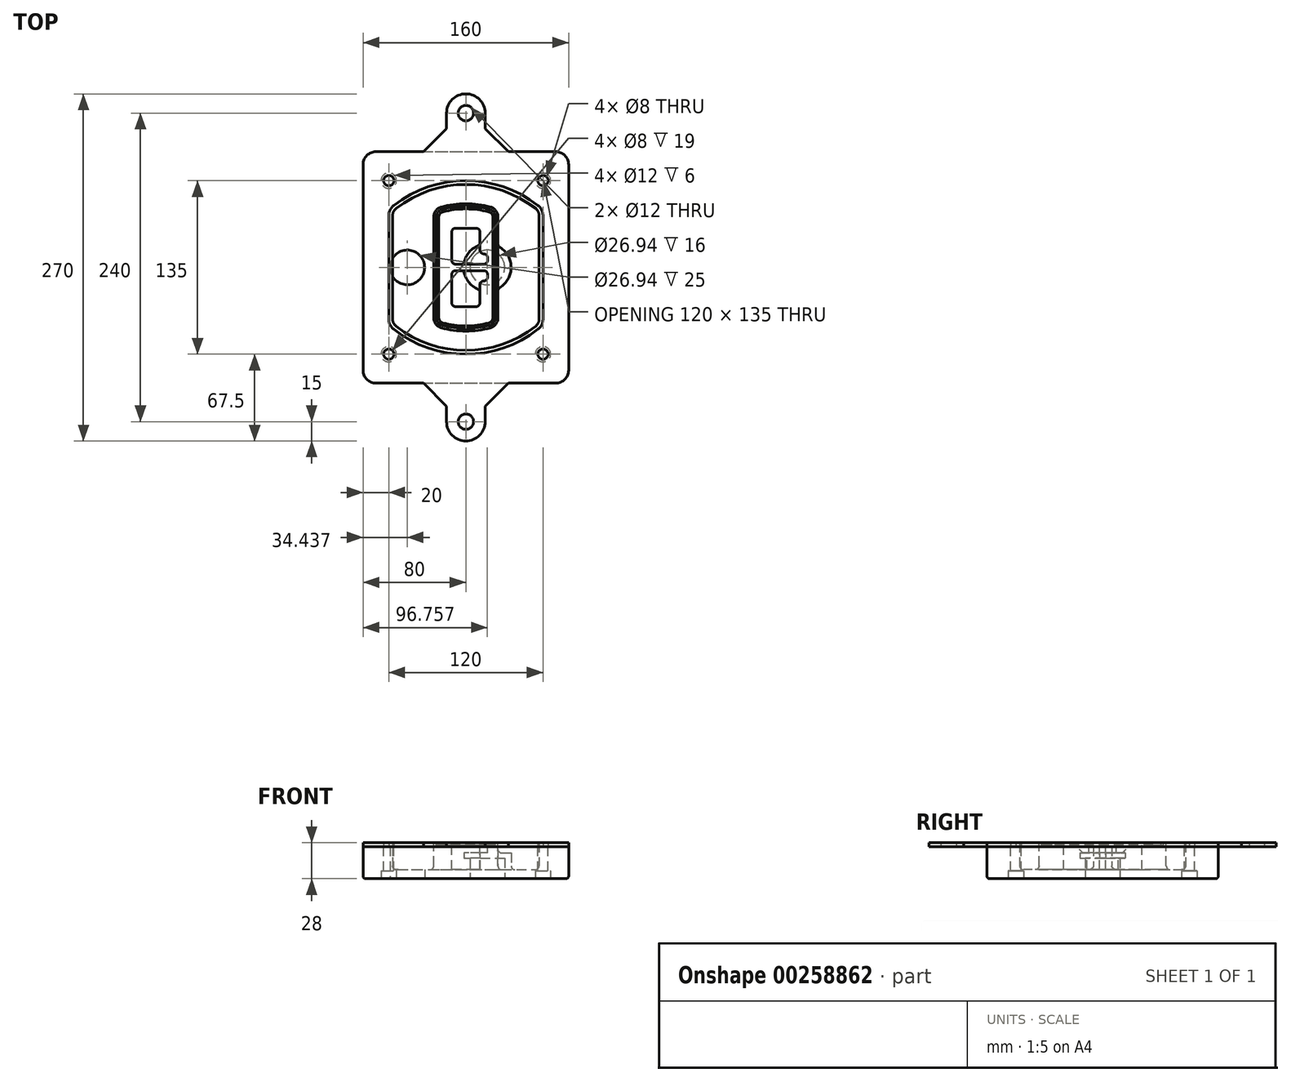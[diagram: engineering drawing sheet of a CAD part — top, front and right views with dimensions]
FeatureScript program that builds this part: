
annotation { "Feature Type Name" : "Feature", "Feature Type Description" : "" }
export const myFeature = defineFeature(function(context is Context, id is Id, definition is map)
    precondition{}
    {
        {
            var Q0;
            Q0=qCreatedBy(makeId("Top.planeOp"),FACE);
            var sketch = newSketch(context, id + "F0", { "sketchPlane" : qUnion([Q0])});
            skPoint(sketch, "E0.rect.middle", {"position": v(0, 0) * mm});
            skLineSegment(sketch, "E1.bottom", {"start": v(-70, -90) * mm, "end": v(70, -90) * mm});
            skLineSegment(sketch, "E1.top", {"start": v(-70, 90) * mm, "end": v(70, 90) * mm});
            skLineSegment(sketch, "E1.left", {"start": v(-80, -80) * mm, "end": v(-80, 80) * mm});
            skLineSegment(sketch, "E1.right", {"start": v(80, -80) * mm, "end": v(80, 80) * mm});
            skLineSegment(sketch, "E2", {"start": v(-80, 90) * mm, "end": v(80, -90) * mm, "construction": true});
            skLineSegment(sketch, "E3", {"start": v(80, 90) * mm, "end": v(-80, -90) * mm, "construction": true});
            skCircle(sketch, "E4", {"center": v(-60, 67.5) * mm, "radius": 4 * mm});
            skCircle(sketch, "E5", {"center": v(60, 67.5) * mm, "radius": 4 * mm});
            skCircle(sketch, "E6", {"center": v(60, -67.5) * mm, "radius": 4 * mm});
            skCircle(sketch, "E7", {"center": v(-60, -67.5) * mm, "radius": 4 * mm});
            skLineSegment(sketch, "E8", {"start": v(-60, 67.5) * mm, "end": v(60, 67.5) * mm, "construction": true});
            skLineSegment(sketch, "E9", {"start": v(60, 67.5) * mm, "end": v(60, -67.5) * mm, "construction": true});
            skLineSegment(sketch, "E10", {"start": v(60, -67.5) * mm, "end": v(-60, -67.5) * mm, "construction": true});
            skLineSegment(sketch, "E11", {"start": v(-60, -67.5) * mm, "end": v(-60, 67.5) * mm, "construction": true});
            skLineSegment(sketch, "E12", {"start": v(-60, 40.3) * mm, "end": v(-60, -40.3) * mm});
            skLineSegment(sketch, "E13", {"start": v(60, 40.3) * mm, "end": v(60, -40.3) * mm});
            skArc(sketch, "E14", {"start": v(56.15, 48.18) * mm, "mid": v(0, 67.5) * mm, "end": v(-56.15, 48.18) * mm});
            skArc(sketch, "E15", {"start": v(-56.15, -48.18) * mm, "mid": v(0, -67.5) * mm, "end": v(56.15, -48.18) * mm});
            skLineSegment(sketch, "E16", {"start": v(-60, 0) * mm, "end": v(60, 0) * mm, "construction": true});
            skPoint(sketch, "E17.visualSharp", {"position": v(-60, -45) * mm});
            skArc(sketch, "E17.filletArc", {"start": v(-60, -40.3) * mm, "mid": v(-58.99, -44.68) * mm, "end": v(-56.15, -48.18) * mm});
            skPoint(sketch, "E18.visualSharp", {"position": v(-60, 45) * mm});
            skArc(sketch, "E18.filletArc", {"start": v(-56.15, 48.18) * mm, "mid": v(-58.99, 44.68) * mm, "end": v(-60, 40.3) * mm});
            skPoint(sketch, "E19.visualSharp", {"position": v(60, 45) * mm});
            skArc(sketch, "E19.filletArc", {"start": v(60, 40.3) * mm, "mid": v(58.99, 44.68) * mm, "end": v(56.15, 48.18) * mm});
            skPoint(sketch, "E20.visualSharp", {"position": v(60, -45) * mm});
            skArc(sketch, "E20.filletArc", {"start": v(56.15, -48.18) * mm, "mid": v(58.99, -44.68) * mm, "end": v(60, -40.3) * mm});
            skPoint(sketch, "E21.visualSharp", {"position": v(-80, 90) * mm});
            skArc(sketch, "E21.filletArc", {"start": v(-70, 90) * mm, "mid": v(-77.07, 87.07) * mm, "end": v(-80, 80) * mm});
            skPoint(sketch, "E22.visualSharp", {"position": v(80, 90) * mm});
            skArc(sketch, "E22.filletArc", {"start": v(80, 80) * mm, "mid": v(77.07, 87.07) * mm, "end": v(70, 90) * mm});
            skPoint(sketch, "E23.visualSharp", {"position": v(80, -90) * mm});
            skArc(sketch, "E23.filletArc", {"start": v(70, -90) * mm, "mid": v(77.07, -87.07) * mm, "end": v(80, -80) * mm});
            skPoint(sketch, "E24.visualSharp", {"position": v(-80, -90) * mm});
            skArc(sketch, "E24.filletArc", {"start": v(-80, -80) * mm, "mid": v(-77.07, -87.07) * mm, "end": v(-70, -90) * mm});
            skArc(sketch, "E25.0", {"start": v(57, 40.3) * mm, "mid": v(56.3, 43.36) * mm, "end": v(54.3, 45.81) * mm});
            skLineSegment(sketch, "E25.1", {"start": v(57, 40.3) * mm, "end": v(57, -40.3) * mm});
            skArc(sketch, "E25.2", {"start": v(54.3, -45.81) * mm, "mid": v(56.3, -43.36) * mm, "end": v(57, -40.3) * mm});
            skArc(sketch, "E25.3", {"start": v(-54.3, -45.81) * mm, "mid": v(0, -64.5) * mm, "end": v(54.3, -45.81) * mm});
            skArc(sketch, "E25.4", {"start": v(-57, -40.3) * mm, "mid": v(-56.3, -43.36) * mm, "end": v(-54.3, -45.81) * mm});
            skArc(sketch, "E25.5", {"start": v(54.3, 45.81) * mm, "mid": v(0, 64.5) * mm, "end": v(-54.3, 45.81) * mm});
            skLineSegment(sketch, "E25.6", {"start": v(-57, 40.3) * mm, "end": v(-57, -40.3) * mm});
            skArc(sketch, "E25.7", {"start": v(-54.3, 45.81) * mm, "mid": v(-56.3, 43.36) * mm, "end": v(-57, 40.3) * mm});
            skArc(sketch, "E26.0", {"start": v(-58.62, 51.33) * mm, "mid": v(-62.58, 46.43) * mm, "end": v(-64, 40.3) * mm});
            skArc(sketch, "E26.1", {"start": v(58.62, 51.33) * mm, "mid": v(0, 71.5) * mm, "end": v(-58.62, 51.33) * mm});
            skArc(sketch, "E26.2", {"start": v(64, 40.3) * mm, "mid": v(62.58, 46.43) * mm, "end": v(58.62, 51.33) * mm});
            skLineSegment(sketch, "E26.3", {"start": v(64, 40.3) * mm, "end": v(64, -40.3) * mm});
            skArc(sketch, "E26.4", {"start": v(58.62, -51.33) * mm, "mid": v(62.58, -46.43) * mm, "end": v(64, -40.3) * mm});
            skLineSegment(sketch, "E26.5", {"start": v(-64, 40.3) * mm, "end": v(-64, -40.3) * mm});
            skArc(sketch, "E26.6", {"start": v(-58.62, -51.33) * mm, "mid": v(0, -71.5) * mm, "end": v(58.62, -51.33) * mm});
            skArc(sketch, "E26.7", {"start": v(-64, -40.3) * mm, "mid": v(-62.58, -46.43) * mm, "end": v(-58.62, -51.33) * mm});
            skSolve(sketch);
        }
        {
            var Q0;
            Q0=makeQuery(id+"F0.imprint","IMPRINT",FACE,{"disambiguationData":[TD([[makeQuery(id+"F0.imprint","IMPRINT",EDGE,{"derivedFrom":sQuery(id+"F0.wireOp",EDGE,"E1.bottom")}),1.0]])]});
            var Q1;
            Q1=makeQuery(id+"F0.imprint","IMPRINT",FACE,{"disambiguationData":[TD([[makeQuery(id+"F0.imprint","IMPRINT",EDGE,{"derivedFrom":sQuery(id+"F0.wireOp",EDGE,"E12")}),1.0]])]});
            var Q2;
            Q2=makeQuery(id+"F0.imprint","IMPRINT",FACE,{"disambiguationData":[TD([[makeQuery(id+"F0.imprint","IMPRINT",EDGE,{"derivedFrom":sQuery(id+"F0.wireOp",EDGE,"E25.0")}),1.0]])]});
            var Q3;
            Q3=makeQuery(id+"F0.imprint","IMPRINT",FACE,{"disambiguationData":[TD([[makeQuery(id+"F0.imprint","IMPRINT",EDGE,{"derivedFrom":sQuery(id+"F0.wireOp",EDGE,"E12")}),-1.0]])]});
            extrude(context, id + "F1", {"entities" : qUnion([Q0, Q1, Q2, Q3]), "oppositeDirection" : true, "depth" : 25 * mm});
        }
        {
            var Q0;
            Q0=makeQuery(id+"F0.imprint","IMPRINT",FACE,{"disambiguationData":[TD([[makeQuery(id+"F0.imprint","IMPRINT",EDGE,{"derivedFrom":sQuery(id+"F0.wireOp",EDGE,"E12")}),1.0]])]});
            extrude(context, id + "F2", {"entities" : qUnion([Q0]), "operationType" : NewBodyOperationType.ADD, "depth" : 3 * mm});
        }
        {
            var Q0;
            Q0=makeQuery(id+"F0.imprint","IMPRINT",FACE,{"disambiguationData":[TD([[makeQuery(id+"F0.imprint","IMPRINT",EDGE,{"derivedFrom":sQuery(id+"F0.wireOp",EDGE,"E25.0")}),1.0]])]});
            extrude(context, id + "F3", {"entities" : qUnion([Q0]), "operationType" : NewBodyOperationType.REMOVE, "oppositeDirection" : true, "depth" : 18 * mm});
        }
        {
            var Q0;
            Q0=makeQuery(id+"F2.opExtrude","CAP_FACE",FACE,{"disambiguationData":[OSD([sQuery(id+"F0.wireOp",EDGE,"E12"),sQuery(id+"F0.wireOp",EDGE,"E13"),sQuery(id+"F0.wireOp",EDGE,"E14"),sQuery(id+"F0.wireOp",EDGE,"E15"),sQuery(id+"F0.wireOp",EDGE,"E17.filletArc"),sQuery(id+"F0.wireOp",EDGE,"E18.filletArc"),sQuery(id+"F0.wireOp",EDGE,"E19.filletArc"),sQuery(id+"F0.wireOp",EDGE,"E20.filletArc"),sQuery(id+"F0.wireOp",EDGE,"E25.0"),sQuery(id+"F0.wireOp",EDGE,"E25.1"),sQuery(id+"F0.wireOp",EDGE,"E25.2"),sQuery(id+"F0.wireOp",EDGE,"E25.3"),sQuery(id+"F0.wireOp",EDGE,"E25.4"),sQuery(id+"F0.wireOp",EDGE,"E25.5"),sQuery(id+"F0.wireOp",EDGE,"E25.6"),sQuery(id+"F0.wireOp",EDGE,"E25.7")])],"isStart":false});
            var sketch = newSketch(context, id + "F4", { "sketchPlane" : qUnion([Q0])});
            skArc(sketch, "E27.0", {"start": v(-19.08, -46.97) * mm, "mid": v(0, -49.5) * mm, "end": v(19.08, -46.97) * mm});
            skArc(sketch, "E28.0", {"start": v(19.08, 46.97) * mm, "mid": v(0, 49.5) * mm, "end": v(-19.08, 46.97) * mm});
            skLineSegment(sketch, "E29", {"start": v(-25, 39.25) * mm, "end": v(-25, -39.25) * mm});
            skLineSegment(sketch, "E30", {"start": v(25, 39.25) * mm, "end": v(25, -39.25) * mm});
            skLineSegment(sketch, "E31", {"start": v(-25, 45.1) * mm, "end": v(25, 45.1) * mm, "construction": true});
            skLineSegment(sketch, "E32", {"start": v(-25, -45.1) * mm, "end": v(25, -45.1) * mm, "construction": true});
            skPoint(sketch, "E33.visualSharp", {"position": v(-25, 45.1) * mm});
            skArc(sketch, "E33.filletArc", {"start": v(-19.08, 46.97) * mm, "mid": v(-23.35, 44.11) * mm, "end": v(-25, 39.25) * mm});
            skPoint(sketch, "E34.visualSharp", {"position": v(25, 45.1) * mm});
            skArc(sketch, "E34.filletArc", {"start": v(25, 39.25) * mm, "mid": v(23.35, 44.11) * mm, "end": v(19.08, 46.97) * mm});
            skPoint(sketch, "E35.visualSharp", {"position": v(25, -45.1) * mm});
            skArc(sketch, "E35.filletArc", {"start": v(19.08, -46.97) * mm, "mid": v(23.35, -44.11) * mm, "end": v(25, -39.25) * mm});
            skPoint(sketch, "E36.visualSharp", {"position": v(-25, -45.1) * mm});
            skArc(sketch, "E36.filletArc", {"start": v(-25, -39.25) * mm, "mid": v(-23.35, -44.11) * mm, "end": v(-19.08, -46.97) * mm});
            skArc(sketch, "E37.0", {"start": v(54.3, 45.81) * mm, "mid": v(0, 64.5) * mm, "end": v(-54.3, 45.81) * mm});
            skArc(sketch, "E37.1", {"start": v(-54.3, 45.81) * mm, "mid": v(-56.3, 43.36) * mm, "end": v(-57, 40.3) * mm});
            skLineSegment(sketch, "E37.2", {"start": v(-57, 40.3) * mm, "end": v(-57, -40.3) * mm});
            skArc(sketch, "E37.3", {"start": v(-57, -40.3) * mm, "mid": v(-56.3, -43.36) * mm, "end": v(-54.3, -45.81) * mm});
            skArc(sketch, "E37.4", {"start": v(-54.3, -45.81) * mm, "mid": v(0, -64.5) * mm, "end": v(54.3, -45.81) * mm});
            skArc(sketch, "E37.5", {"start": v(54.3, -45.81) * mm, "mid": v(56.3, -43.36) * mm, "end": v(57, -40.3) * mm});
            skLineSegment(sketch, "E37.6", {"start": v(57, 40.3) * mm, "end": v(57, -40.3) * mm});
            skArc(sketch, "E37.7", {"start": v(57, 40.3) * mm, "mid": v(56.3, 43.36) * mm, "end": v(54.3, 45.81) * mm});
            skLineSegment(sketch, "E38.0", {"start": v(23, 39.25) * mm, "end": v(23, -39.25) * mm});
            skArc(sketch, "E38.1", {"start": v(18.56, -45.04) * mm, "mid": v(21.76, -42.9) * mm, "end": v(23, -39.25) * mm});
            skArc(sketch, "E38.2", {"start": v(-18.56, -45.04) * mm, "mid": v(0, -47.5) * mm, "end": v(18.56, -45.04) * mm});
            skArc(sketch, "E38.3", {"start": v(-23, -39.25) * mm, "mid": v(-21.76, -42.9) * mm, "end": v(-18.56, -45.04) * mm});
            skLineSegment(sketch, "E38.4", {"start": v(-23, 39.25) * mm, "end": v(-23, -39.25) * mm});
            skArc(sketch, "E38.5", {"start": v(23, 39.25) * mm, "mid": v(21.76, 42.9) * mm, "end": v(18.56, 45.04) * mm});
            skArc(sketch, "E38.6", {"start": v(-18.56, 45.04) * mm, "mid": v(-21.76, 42.9) * mm, "end": v(-23, 39.25) * mm});
            skArc(sketch, "E38.7", {"start": v(18.56, 45.04) * mm, "mid": v(0, 47.5) * mm, "end": v(-18.56, 45.04) * mm});
            skArc(sketch, "E39.0", {"start": v(21, 39.25) * mm, "mid": v(20.18, 41.68) * mm, "end": v(18.04, 43.1) * mm});
            skLineSegment(sketch, "E39.1", {"start": v(21, 39.25) * mm, "end": v(21, -39.25) * mm});
            skArc(sketch, "E39.2", {"start": v(18.04, -43.1) * mm, "mid": v(20.18, -41.68) * mm, "end": v(21, -39.25) * mm});
            skArc(sketch, "E39.3", {"start": v(-18.04, -43.1) * mm, "mid": v(0, -45.5) * mm, "end": v(18.04, -43.1) * mm});
            skArc(sketch, "E39.4", {"start": v(-21, -39.25) * mm, "mid": v(-20.18, -41.68) * mm, "end": v(-18.04, -43.1) * mm});
            skArc(sketch, "E39.5", {"start": v(18.04, 43.1) * mm, "mid": v(0, 45.5) * mm, "end": v(-18.04, 43.1) * mm});
            skLineSegment(sketch, "E39.6", {"start": v(-21, 39.25) * mm, "end": v(-21, -39.25) * mm});
            skArc(sketch, "E39.7", {"start": v(-18.04, 43.1) * mm, "mid": v(-20.18, 41.68) * mm, "end": v(-21, 39.25) * mm});
            skLineSegment(sketch, "E40", {"start": v(-25, 0) * mm, "end": v(25, 0) * mm, "construction": true});
            skLineSegment(sketch, "E41", {"start": v(-11, 5.5) * mm, "end": v(-11, 27.5) * mm});
            skLineSegment(sketch, "E42", {"start": v(-8, 30.5) * mm, "end": v(8, 30.5) * mm});
            skLineSegment(sketch, "E43", {"start": v(11, 27.5) * mm, "end": v(11, 13.5) * mm});
            skLineSegment(sketch, "E44", {"start": v(14, 10.5) * mm, "end": v(14, 10.5) * mm});
            skLineSegment(sketch, "E45", {"start": v(17, 7.5) * mm, "end": v(17, 5.5) * mm});
            skLineSegment(sketch, "E46", {"start": v(14, 2.5) * mm, "end": v(-8, 2.5) * mm});
            skPoint(sketch, "E47.visualSharp", {"position": v(-11, 30.5) * mm});
            skArc(sketch, "E47.filletArc", {"start": v(-8, 30.5) * mm, "mid": v(-10.12, 29.62) * mm, "end": v(-11, 27.5) * mm});
            skPoint(sketch, "E48.visualSharp", {"position": v(11, 30.5) * mm});
            skArc(sketch, "E48.filletArc", {"start": v(11, 27.5) * mm, "mid": v(10.12, 29.62) * mm, "end": v(8, 30.5) * mm});
            skPoint(sketch, "E49.visualSharp", {"position": v(11, 10.5) * mm});
            skArc(sketch, "E49.filletArc", {"start": v(11, 13.5) * mm, "mid": v(11.88, 11.38) * mm, "end": v(14, 10.5) * mm});
            skPoint(sketch, "E50.visualSharp", {"position": v(17, 10.5) * mm});
            skArc(sketch, "E50.filletArc", {"start": v(17, 7.5) * mm, "mid": v(16.12, 9.62) * mm, "end": v(14, 10.5) * mm});
            skPoint(sketch, "E51.visualSharp", {"position": v(17, 2.5) * mm});
            skArc(sketch, "E51.filletArc", {"start": v(14, 2.5) * mm, "mid": v(16.12, 3.38) * mm, "end": v(17, 5.5) * mm});
            skPoint(sketch, "E52.visualSharp", {"position": v(-11, 2.5) * mm});
            skArc(sketch, "E52.filletArc", {"start": v(-11, 5.5) * mm, "mid": v(-10.12, 3.38) * mm, "end": v(-8, 2.5) * mm});
            skLineSegment(sketch, "E53.0.MirrorCS", {"start": v(14, -2.5) * mm, "end": v(-8, -2.5) * mm});
            skArc(sketch, "E54.0.MirrorCS", {"start": v(-11, -5.5) * mm, "mid": v(-10.12, -3.38) * mm, "end": v(-8, -2.5) * mm});
            skLineSegment(sketch, "E55.0.MirrorCS", {"start": v(-11, -5.5) * mm, "end": v(-11, -27.5) * mm});
            skArc(sketch, "E56.0.MirrorCS", {"start": v(-8, -30.5) * mm, "mid": v(-10.12, -29.62) * mm, "end": v(-11, -27.5) * mm});
            skLineSegment(sketch, "E57.0.MirrorCS", {"start": v(-8, -30.5) * mm, "end": v(8, -30.5) * mm});
            skArc(sketch, "E58.0.MirrorCS", {"start": v(11, -27.5) * mm, "mid": v(10.12, -29.62) * mm, "end": v(8, -30.5) * mm});
            skLineSegment(sketch, "E59.0.MirrorCS", {"start": v(11, -27.5) * mm, "end": v(11, -13.5) * mm});
            skArc(sketch, "E60.0.MirrorCS", {"start": v(11, -13.5) * mm, "mid": v(11.88, -11.38) * mm, "end": v(14, -10.5) * mm});
            skArc(sketch, "E61.0.MirrorCS", {"start": v(17, -7.5) * mm, "mid": v(16.12, -9.62) * mm, "end": v(14, -10.5) * mm});
            skLineSegment(sketch, "E62.0.MirrorCS", {"start": v(17, -7.5) * mm, "end": v(17, -5.5) * mm});
            skArc(sketch, "E63.0.MirrorCS", {"start": v(14, -2.5) * mm, "mid": v(16.12, -3.38) * mm, "end": v(17, -5.5) * mm});
            skSolve(sketch);
        }
        {
            var Q0;
            Q0=makeQuery(id+"F4.imprint","IMPRINT",FACE,{"disambiguationData":[TD([[makeQuery(id+"F4.imprint","IMPRINT",EDGE,{"derivedFrom":sQuery(id+"F4.wireOp",EDGE,"E27.0")}),1.0]])]});
            var Q1;
            Q1=makeQuery(id+"F4.imprint","IMPRINT",FACE,{"disambiguationData":[TD([[makeQuery(id+"F4.imprint","IMPRINT",EDGE,{"derivedFrom":sQuery(id+"F4.wireOp",EDGE,"E38.0")}),-1.0]])]});
            var Q2;
            Q2=makeQuery(id+"F4.imprint","IMPRINT",FACE,{"disambiguationData":[TD([[makeQuery(id+"F4.imprint","IMPRINT",EDGE,{"derivedFrom":sQuery(id+"F4.wireOp",EDGE,"E39.0")}),1.0]])]});
            extrude(context, id + "F5", {"entities" : qUnion([Q0, Q1, Q2]), "operationType" : NewBodyOperationType.ADD, "endBound" : BoundingType.UP_TO_NEXT, "oppositeDirection" : true, "depth" : 25 * mm});
        }
        {
            var Q0;
            Q0=makeQuery(id+"F4.imprint","IMPRINT",FACE,{"disambiguationData":[TD([[makeQuery(id+"F4.imprint","IMPRINT",EDGE,{"derivedFrom":sQuery(id+"F4.wireOp",EDGE,"E38.0")}),-1.0]])]});
            extrude(context, id + "F6", {"entities" : qUnion([Q0]), "operationType" : NewBodyOperationType.REMOVE, "oppositeDirection" : true, "depth" : 2 * mm});
        }
        {
            var Q0;
            Q0=makeQuery(id+"F1.opExtrude","CAP_FACE",FACE,{"disambiguationData":[OSD([sQuery(id+"F0.wireOp",EDGE,"E1.bottom"),sQuery(id+"F0.wireOp",EDGE,"E1.top"),sQuery(id+"F0.wireOp",EDGE,"E1.left"),sQuery(id+"F0.wireOp",EDGE,"E1.right"),sQuery(id+"F0.wireOp",EDGE,"E4"),sQuery(id+"F0.wireOp",EDGE,"E5"),sQuery(id+"F0.wireOp",EDGE,"E6"),sQuery(id+"F0.wireOp",EDGE,"E7"),sQuery(id+"F0.wireOp",EDGE,"E21.filletArc"),sQuery(id+"F0.wireOp",EDGE,"E22.filletArc"),sQuery(id+"F0.wireOp",EDGE,"E23.filletArc"),sQuery(id+"F0.wireOp",EDGE,"E24.filletArc")])],"isStart":false});
            var sketch = newSketch(context, id + "F7", { "sketchPlane" : qUnion([Q0])});
            skCircle(sketch, "E64", {"center": v(16.76, 0) * mm, "radius": 13.47 * mm});
            skCircle(sketch, "E65", {"center": v(-45.56, 0) * mm, "radius": 13.47 * mm});
            skLineSegment(sketch, "E66", {"start": v(80, 0) * mm, "end": v(-80, 0) * mm});
            skCircle(sketch, "E67", {"center": v(16.76, 0) * mm, "radius": 18.47 * mm});
            skCircle(sketch, "E68", {"center": v(60, -67.5) * mm, "radius": 6 * mm});
            skCircle(sketch, "E69", {"center": v(-60, -67.5) * mm, "radius": 6 * mm});
            skCircle(sketch, "E70", {"center": v(-60, 67.5) * mm, "radius": 6 * mm});
            skCircle(sketch, "E71", {"center": v(60, 67.5) * mm, "radius": 6 * mm});
            skSolve(sketch);
        }
        {
            var Q0;
            {var subQ1=sQuery(id+"F7.wireOp",EDGE,"E66");var subQ4=sQuery(id+"F7.wireOp",EDGE,"E64");var subQ6=makeQuery(id+"F7.imprint","INTERSECT",VERTEX,{"disambiguationData":[OD(0.0)],"derivedFrom":[subQ4,subQ1]});Q0=makeQuery(id+"F7.imprint","IMPRINT",FACE,{"disambiguationData":[TD([[makeQuery(id+"F7.imprint","IMPRINT",EDGE,{"disambiguationData":[TD([[subQ6,-1.0]])],"derivedFrom":subQ4}),-1.0]])]});}
            var Q1;
            {var subQ0=sQuery(id+"F7.wireOp",EDGE,"E66");var subQ1=sQuery(id+"F7.wireOp",EDGE,"E64");var subQ3=makeQuery(id+"F7.imprint","INTERSECT",VERTEX,{"disambiguationData":[OD(0.0)],"derivedFrom":[subQ1,subQ0]});Q1=makeQuery(id+"F7.imprint","IMPRINT",FACE,{"disambiguationData":[TD([[makeQuery(id+"F7.imprint","IMPRINT",EDGE,{"disambiguationData":[TD([[subQ3,-1.0]])],"derivedFrom":subQ1}),1.0]])]});}
            var Q2;
            {var subQ0=sQuery(id+"F7.wireOp",EDGE,"E66");var subQ1=sQuery(id+"F7.wireOp",EDGE,"E64");var subQ3=makeQuery(id+"F7.imprint","INTERSECT",VERTEX,{"disambiguationData":[OD(0.0)],"derivedFrom":[subQ1,subQ0]});Q2=makeQuery(id+"F7.imprint","IMPRINT",FACE,{"disambiguationData":[TD([[makeQuery(id+"F7.imprint","IMPRINT",EDGE,{"disambiguationData":[TD([[subQ3,1.0]])],"derivedFrom":subQ1}),1.0]])]});}
            var Q3;
            {var subQ1=sQuery(id+"F7.wireOp",EDGE,"E66");var subQ4=sQuery(id+"F7.wireOp",EDGE,"E64");var subQ6=makeQuery(id+"F7.imprint","INTERSECT",VERTEX,{"disambiguationData":[OD(0.0)],"derivedFrom":[subQ4,subQ1]});Q3=makeQuery(id+"F7.imprint","IMPRINT",FACE,{"disambiguationData":[TD([[makeQuery(id+"F7.imprint","IMPRINT",EDGE,{"disambiguationData":[TD([[subQ6,1.0]])],"derivedFrom":subQ4}),-1.0]])]});}
            extrude(context, id + "F8", {"entities" : qUnion([Q0, Q1, Q2, Q3]), "operationType" : NewBodyOperationType.ADD, "oppositeDirection" : true, "depth" : 20 * mm});
        }
        {
            var Q0;
            {var subQ0=sQuery(id+"F7.wireOp",EDGE,"E66");var subQ1=sQuery(id+"F7.wireOp",EDGE,"E64");var subQ3=makeQuery(id+"F7.imprint","INTERSECT",VERTEX,{"disambiguationData":[OD(0.0)],"derivedFrom":[subQ1,subQ0]});Q0=makeQuery(id+"F7.imprint","IMPRINT",FACE,{"disambiguationData":[TD([[makeQuery(id+"F7.imprint","IMPRINT",EDGE,{"disambiguationData":[TD([[subQ3,-1.0]])],"derivedFrom":subQ1}),1.0]])]});}
            var Q1;
            {var subQ0=sQuery(id+"F7.wireOp",EDGE,"E66");var subQ1=sQuery(id+"F7.wireOp",EDGE,"E64");var subQ3=makeQuery(id+"F7.imprint","INTERSECT",VERTEX,{"disambiguationData":[OD(0.0)],"derivedFrom":[subQ1,subQ0]});Q1=makeQuery(id+"F7.imprint","IMPRINT",FACE,{"disambiguationData":[TD([[makeQuery(id+"F7.imprint","IMPRINT",EDGE,{"disambiguationData":[TD([[subQ3,1.0]])],"derivedFrom":subQ1}),1.0]])]});}
            extrude(context, id + "F9", {"entities" : qUnion([Q0, Q1]), "operationType" : NewBodyOperationType.REMOVE, "oppositeDirection" : true, "depth" : 16 * mm});
        }
        {
            var Q0;
            {var subQ0=sQuery(id+"F7.wireOp",EDGE,"E66");var subQ1=sQuery(id+"F7.wireOp",EDGE,"E65");var subQ3=makeQuery(id+"F7.imprint","INTERSECT",VERTEX,{"disambiguationData":[OD(0.0)],"derivedFrom":[subQ1,subQ0]});Q0=makeQuery(id+"F7.imprint","IMPRINT",FACE,{"disambiguationData":[TD([[makeQuery(id+"F7.imprint","IMPRINT",EDGE,{"disambiguationData":[TD([[subQ3,-1.0]])],"derivedFrom":subQ1}),1.0]])]});}
            var Q1;
            {var subQ0=sQuery(id+"F7.wireOp",EDGE,"E66");var subQ1=sQuery(id+"F7.wireOp",EDGE,"E65");var subQ3=makeQuery(id+"F7.imprint","INTERSECT",VERTEX,{"disambiguationData":[OD(0.0)],"derivedFrom":[subQ1,subQ0]});Q1=makeQuery(id+"F7.imprint","IMPRINT",FACE,{"disambiguationData":[TD([[makeQuery(id+"F7.imprint","IMPRINT",EDGE,{"disambiguationData":[TD([[subQ3,1.0]])],"derivedFrom":subQ1}),1.0]])]});}
            extrude(context, id + "F10", {"entities" : qUnion([Q0, Q1]), "operationType" : NewBodyOperationType.REMOVE, "oppositeDirection" : true, "depth" : 25 * mm});
        }
        {
            var Q0;
            Q0=makeQuery(id+"F7.imprint","IMPRINT",FACE,{"disambiguationData":[TD([[makeQuery(id+"F7.imprint","IMPRINT",EDGE,{"derivedFrom":sQuery(id+"F7.wireOp",EDGE,"E68")}),1.0]])]});
            var Q1;
            Q1=makeQuery(id+"F7.imprint","IMPRINT",FACE,{"disambiguationData":[TD([[makeQuery(id+"F7.imprint","IMPRINT",EDGE,{"derivedFrom":makeQuery(id+"F1.opExtrude","CAP_EDGE",EDGE,{"disambiguationData":[OSD([sQuery(id+"F0.wireOp",EDGE,"E5")])],"isStart":false})}),-1.0]])]});
            var Q2;
            Q2=makeQuery(id+"F7.imprint","IMPRINT",FACE,{"disambiguationData":[TD([[makeQuery(id+"F7.imprint","IMPRINT",EDGE,{"derivedFrom":sQuery(id+"F7.wireOp",EDGE,"E69")}),1.0]])]});
            var Q3;
            Q3=makeQuery(id+"F7.imprint","IMPRINT",FACE,{"disambiguationData":[TD([[makeQuery(id+"F7.imprint","IMPRINT",EDGE,{"derivedFrom":makeQuery(id+"F1.opExtrude","CAP_EDGE",EDGE,{"disambiguationData":[OSD([sQuery(id+"F0.wireOp",EDGE,"E4")])],"isStart":false})}),-1.0]])]});
            var Q4;
            Q4=makeQuery(id+"F7.imprint","IMPRINT",FACE,{"disambiguationData":[TD([[makeQuery(id+"F7.imprint","IMPRINT",EDGE,{"derivedFrom":sQuery(id+"F7.wireOp",EDGE,"E70")}),1.0]])]});
            var Q5;
            Q5=makeQuery(id+"F7.imprint","IMPRINT",FACE,{"disambiguationData":[TD([[makeQuery(id+"F7.imprint","IMPRINT",EDGE,{"derivedFrom":makeQuery(id+"F1.opExtrude","CAP_EDGE",EDGE,{"disambiguationData":[OSD([sQuery(id+"F0.wireOp",EDGE,"E7")])],"isStart":false})}),-1.0]])]});
            var Q6;
            Q6=makeQuery(id+"F7.imprint","IMPRINT",FACE,{"disambiguationData":[TD([[makeQuery(id+"F7.imprint","IMPRINT",EDGE,{"derivedFrom":sQuery(id+"F7.wireOp",EDGE,"E71")}),1.0]])]});
            var Q7;
            Q7=makeQuery(id+"F7.imprint","IMPRINT",FACE,{"disambiguationData":[TD([[makeQuery(id+"F7.imprint","IMPRINT",EDGE,{"derivedFrom":makeQuery(id+"F1.opExtrude","CAP_EDGE",EDGE,{"disambiguationData":[OSD([sQuery(id+"F0.wireOp",EDGE,"E6")])],"isStart":false})}),-1.0]])]});
            extrude(context, id + "F11", {"entities" : qUnion([Q0, Q1, Q2, Q3, Q4, Q5, Q6, Q7]), "operationType" : NewBodyOperationType.REMOVE, "oppositeDirection" : true, "depth" : 6 * mm});
        }
        {
            var Q0;
            Q0=makeQuery(id+"F9.boolean.opBoolean","COPY",FACE,{"derivedFrom":makeQuery(id+"F9.opExtrude","CAP_FACE",FACE,{"disambiguationData":[OSD([sQuery(id+"F7.wireOp",EDGE,"E64")])],"isStart":false})});
            var sketch = newSketch(context, id + "F12", { "sketchPlane" : qUnion([Q0])});
            skArc(sketch, "E72.0", {"start": v(11, 17.55) * mm, "mid": v(2.57, 11.82) * mm, "end": v(-1.54, 2.5) * mm});
            skArc(sketch, "E72.1", {"start": v(-1.54, -2.5) * mm, "mid": v(2.57, -11.82) * mm, "end": v(11, -17.55) * mm});
            skLineSegment(sketch, "E73", {"start": v(-1.54, -2.5) * mm, "end": v(14, -2.5) * mm});
            skLineSegment(sketch, "E74.0", {"start": v(14, 2.5) * mm, "end": v(-1.54, 2.5) * mm});
            skArc(sketch, "E74.1", {"start": v(14, 2.5) * mm, "mid": v(16.12, 3.38) * mm, "end": v(17, 5.5) * mm});
            skLineSegment(sketch, "E74.2", {"start": v(17, 7.5) * mm, "end": v(17, 5.5) * mm});
            skArc(sketch, "E74.3", {"start": v(17, 7.5) * mm, "mid": v(16.12, 9.62) * mm, "end": v(14, 10.5) * mm});
            skArc(sketch, "E74.4", {"start": v(11, 13.5) * mm, "mid": v(11.88, 11.38) * mm, "end": v(14, 10.5) * mm});
            skLineSegment(sketch, "E74.5", {"start": v(11, 17.55) * mm, "end": v(11, 13.5) * mm});
            skLineSegment(sketch, "E74.7", {"start": v(14, -2.5) * mm, "end": v(-1.54, -2.5) * mm});
            skArc(sketch, "E74.8", {"start": v(14, -2.5) * mm, "mid": v(16.12, -3.38) * mm, "end": v(17, -5.5) * mm});
            skLineSegment(sketch, "E74.9", {"start": v(17, -7.5) * mm, "end": v(17, -5.5) * mm});
            skArc(sketch, "E74.10", {"start": v(17, -7.5) * mm, "mid": v(16.12, -9.62) * mm, "end": v(14, -10.5) * mm});
            skArc(sketch, "E74.11", {"start": v(11, -13.5) * mm, "mid": v(11.88, -11.38) * mm, "end": v(14, -10.5) * mm});
            skLineSegment(sketch, "E74.12", {"start": v(11, -17.55) * mm, "end": v(11, -13.5) * mm});
            skPoint(sketch, "E75.orphan", {"position": v(11, -27.5) * mm});
            skPoint(sketch, "E76.orphan", {"position": v(-8, -2.5) * mm});
            skPoint(sketch, "E77.orphan", {"position": v(-8, 2.5) * mm});
            skPoint(sketch, "E78.orphan", {"position": v(11, 27.5) * mm});
            skSolve(sketch);
        }
        {
            var Q0;
            {var subQ7=sQuery(id+"F12.wireOp",EDGE,"E72.0");var subQ14=sQuery(id+"F12.wireOp",EDGE,"E72.1");var subQ16=sQuery(id+"F12.wireOp",EDGE,"E74.1");var subQ18=sQuery(id+"F12.wireOp",EDGE,"E74.8");Q0=qUnion([makeQuery(id+"F12.imprint","IMPRINT",FACE,{"disambiguationData":[TD([[makeQuery(id+"F12.imprint","IMPRINT",EDGE,{"derivedFrom":subQ7}),1.0]])]}),makeQuery(id+"F12.imprint","IMPRINT",FACE,{"disambiguationData":[TD([[makeQuery(id+"F12.imprint","IMPRINT",EDGE,{"derivedFrom":subQ14}),1.0]])]}),makeQuery(id+"F12.imprint","IMPRINT",FACE,{"disambiguationData":[TD([[makeQuery(id+"F12.imprint","IMPRINT",EDGE,{"derivedFrom":subQ16}),1.0]])]}),makeQuery(id+"F12.imprint","IMPRINT",FACE,{"disambiguationData":[TD([[makeQuery(id+"F12.imprint","IMPRINT",EDGE,{"derivedFrom":subQ18}),-1.0]])]})]);}
            var Q1;
            Q1=makeQuery(id+"F5.boolean.opBoolean","SPLIT",FACE,{"disambiguationData":[TD([makeQuery(id+"F5.opExtrude","SWEPT_FACE",FACE,{"disambiguationData":[OSD([sQuery(id+"F4.wireOp",EDGE,"E41")])]})])],"derivedFrom":makeQuery(id+"F3.boolean.opBoolean","COPY",FACE,{"derivedFrom":makeQuery(id+"F3.opExtrude","CAP_FACE",FACE,{"disambiguationData":[OSD([sQuery(id+"F0.wireOp",EDGE,"E25.0"),sQuery(id+"F0.wireOp",EDGE,"E25.1"),sQuery(id+"F0.wireOp",EDGE,"E25.2"),sQuery(id+"F0.wireOp",EDGE,"E25.3"),sQuery(id+"F0.wireOp",EDGE,"E25.4"),sQuery(id+"F0.wireOp",EDGE,"E25.5"),sQuery(id+"F0.wireOp",EDGE,"E25.6"),sQuery(id+"F0.wireOp",EDGE,"E25.7")])],"isStart":false})})});
            extrude(context, id + "F13", {"entities" : qUnion([Q0]), "operationType" : NewBodyOperationType.REMOVE, "endBound" : BoundingType.UP_TO_SURFACE, "endBoundEntityFace" : qUnion([Q1]), "depth" : 25 * mm});
        }
        {
            var Q0;
            Q0=makeQuery(id+"F3.boolean.opBoolean","COPY",EDGE,{"derivedFrom":makeQuery(id+"F3.opExtrude","CAP_EDGE",EDGE,{"disambiguationData":[OSD([sQuery(id+"F0.wireOp",EDGE,"E25.6")])],"isStart":false})});
            var Q1;
            Q1=makeQuery(id+"F8.boolean.opBoolean","INTERSECT",EDGE,{"derivedFrom":[makeQuery(id+"F5.opExtrude","SWEPT_FACE",FACE,{"disambiguationData":[OSD([sQuery(id+"F4.wireOp",EDGE,"E30")])]}),makeQuery(id+"F8.opExtrude","CAP_FACE",FACE,{"disambiguationData":[OSD([sQuery(id+"F7.wireOp",EDGE,"E67")])],"isStart":false})]});
            var Q2;
            Q2=makeQuery(id+"F8.boolean.opBoolean","INTERSECT",EDGE,{"disambiguationData":[OD(1.0)],"derivedFrom":[makeQuery(id+"F5.opExtrude","SWEPT_FACE",FACE,{"disambiguationData":[OSD([sQuery(id+"F4.wireOp",EDGE,"E30")])]}),makeQuery(id+"F8.opExtrude","SWEPT_FACE",FACE,{"disambiguationData":[OSD([sQuery(id+"F7.wireOp",EDGE,"E67")])]})]});
            var Q3;
            {var subQ0=sQuery(id+"F4.wireOp",EDGE,"E30");Q3=makeQuery(id+"F8.boolean.opBoolean","SPLIT",EDGE,{"disambiguationData":[TD([makeQuery(id+"F5.opExtrude","SWEPT_FACE",FACE,{"disambiguationData":[OSD([sQuery(id+"F4.wireOp",EDGE,"E35.filletArc")])]})])],"derivedFrom":makeQuery(id+"F5.opExtrude","CAP_EDGE",EDGE,{"disambiguationData":[OSD([subQ0])],"isStart":false})});}
            var Q4;
            {var subQ0=sQuery(id+"F0.wireOp",EDGE,"E25.7");var subQ1=sQuery(id+"F0.wireOp",EDGE,"E25.1");var subQ2=sQuery(id+"F0.wireOp",EDGE,"E25.6");var subQ3=sQuery(id+"F0.wireOp",EDGE,"E25.5");var subQ4=sQuery(id+"F0.wireOp",EDGE,"E25.4");var subQ5=sQuery(id+"F0.wireOp",EDGE,"E25.0");var subQ6=sQuery(id+"F0.wireOp",EDGE,"E25.2");var subQ7=sQuery(id+"F0.wireOp",EDGE,"E25.3");Q4=makeQuery(id+"F8.boolean.opBoolean","INTERSECT",EDGE,{"derivedFrom":[makeQuery(id+"F5.boolean.opBoolean","SPLIT",FACE,{"disambiguationData":[TD([makeQuery(id+"F2.opExtrude","SWEPT_FACE",FACE,{"disambiguationData":[OSD([subQ5])]})])],"derivedFrom":makeQuery(id+"F3.boolean.opBoolean","COPY",FACE,{"derivedFrom":makeQuery(id+"F3.opExtrude","CAP_FACE",FACE,{"disambiguationData":[OSD([subQ5,subQ1,subQ6,subQ7,subQ4,subQ3,subQ2,subQ0])],"isStart":false})})}),makeQuery(id+"F8.opExtrude","SWEPT_FACE",FACE,{"disambiguationData":[OSD([sQuery(id+"F7.wireOp",EDGE,"E67")])]})]});}
            var Q5;
            Q5=makeQuery(id+"F8.boolean.opBoolean","INTERSECT",EDGE,{"disambiguationData":[OD(0.0)],"derivedFrom":[makeQuery(id+"F5.opExtrude","SWEPT_FACE",FACE,{"disambiguationData":[OSD([sQuery(id+"F4.wireOp",EDGE,"E30")])]}),makeQuery(id+"F8.opExtrude","SWEPT_FACE",FACE,{"disambiguationData":[OSD([sQuery(id+"F7.wireOp",EDGE,"E67")])]})]});
            fillet(context, id + "F14", {"entities" : qUnion([Q0, Q1, Q2, Q3, Q4, Q5]), "radius" : 3 * mm, "tangentPropagation" : true, "allowEdgeOverflow" : false});
        }
        {
            var Q0;
            Q0=makeQuery(id+"F1.opExtrude","CAP_EDGE",EDGE,{"disambiguationData":[OSD([sQuery(id+"F0.wireOp",EDGE,"E1.bottom")])],"isStart":false});
            fillet(context, id + "F15", {"entities" : qUnion([Q0]), "radius" : 2 * mm, "tangentPropagation" : true, "allowEdgeOverflow" : false});
        }
        {
            var Q0;
            {var subQ0=sQuery(id+"F0.wireOp",EDGE,"E22.filletArc");var subQ1=sQuery(id+"F0.wireOp",EDGE,"E7");var subQ2=sQuery(id+"F0.wireOp",EDGE,"E6");var subQ3=sQuery(id+"F0.wireOp",EDGE,"E5");var subQ4=sQuery(id+"F0.wireOp",EDGE,"E4");var subQ5=sQuery(id+"F0.wireOp",EDGE,"E1.bottom");var subQ6=sQuery(id+"F0.wireOp",EDGE,"E21.filletArc");var subQ7=sQuery(id+"F0.wireOp",EDGE,"E1.top");var subQ8=sQuery(id+"F0.wireOp",EDGE,"E1.left");var subQ9=sQuery(id+"F0.wireOp",EDGE,"E1.right");var subQ10=sQuery(id+"F0.wireOp",EDGE,"E23.filletArc");var subQ11=sQuery(id+"F0.wireOp",EDGE,"E24.filletArc");Q0=makeQuery(id+"F2.boolean.opBoolean","SPLIT",FACE,{"disambiguationData":[TD([makeQuery(id+"F1.opExtrude","SWEPT_FACE",FACE,{"disambiguationData":[OSD([subQ5])]})])],"derivedFrom":makeQuery(id+"F1.opExtrude","CAP_FACE",FACE,{"disambiguationData":[OSD([subQ5,subQ7,subQ8,subQ9,subQ4,subQ3,subQ2,subQ1,subQ6,subQ0,subQ10,subQ11])],"isStart":true})});}
            var sketch = newSketch(context, id + "F16", { "sketchPlane" : qUnion([Q0])});
            skLineSegment(sketch, "E79.0.0", {"start": v(70, 90) * mm, "end": v(-70, 90) * mm});
            skArc(sketch, "E79.0.1", {"start": v(-70, 90) * mm, "mid": v(-77.07, 87.07) * mm, "end": v(-80, 80) * mm});
            skLineSegment(sketch, "E79.0.2", {"start": v(-80, 80) * mm, "end": v(-80, -80) * mm});
            skArc(sketch, "E79.0.3", {"start": v(-80, -80) * mm, "mid": v(-77.07, -87.07) * mm, "end": v(-70, -90) * mm});
            skLineSegment(sketch, "E79.0.4", {"start": v(-70, -90) * mm, "end": v(70, -90) * mm});
            skArc(sketch, "E79.0.5", {"start": v(70, -90) * mm, "mid": v(77.07, -87.07) * mm, "end": v(80, -80) * mm});
            skLineSegment(sketch, "E79.0.6", {"start": v(80, -80) * mm, "end": v(80, 80) * mm});
            skArc(sketch, "E79.0.7", {"start": v(80, 80) * mm, "mid": v(77.07, 87.07) * mm, "end": v(70, 90) * mm});
            skArc(sketch, "E80.0", {"start": v(56.15, 48.18) * mm, "mid": v(0, 67.5) * mm, "end": v(-56.15, 48.18) * mm});
            skArc(sketch, "E81.0", {"start": v(-56.15, 48.18) * mm, "mid": v(-58.99, 44.68) * mm, "end": v(-60, 40.3) * mm});
            skLineSegment(sketch, "E82.0", {"start": v(-60, 40.3) * mm, "end": v(-60, -40.3) * mm});
            skArc(sketch, "E83.0", {"start": v(-60, -40.3) * mm, "mid": v(-58.99, -44.68) * mm, "end": v(-56.15, -48.18) * mm});
            skArc(sketch, "E84.0", {"start": v(-56.15, -48.18) * mm, "mid": v(0, -67.5) * mm, "end": v(56.15, -48.18) * mm});
            skArc(sketch, "E85.0", {"start": v(56.15, -48.18) * mm, "mid": v(58.99, -44.68) * mm, "end": v(60, -40.3) * mm});
            skLineSegment(sketch, "E86.0", {"start": v(60, 40.3) * mm, "end": v(60, -40.3) * mm});
            skLineSegment(sketch, "E87", {"start": v(0, 90) * mm, "end": v(0, 120) * mm, "construction": true});
            skCircle(sketch, "E88", {"center": v(0, 120) * mm, "radius": 6 * mm});
            skLineSegment(sketch, "E89", {"start": v(-33, 90) * mm, "end": v(-15, 108) * mm});
            skLineSegment(sketch, "E90", {"start": v(-15, 108) * mm, "end": v(-15, 120) * mm});
            skArc(sketch, "E91", {"start": v(-15, 120) * mm, "mid": v(0, 135) * mm, "end": v(15, 120) * mm});
            skLineSegment(sketch, "E92", {"start": v(15, 120) * mm, "end": v(15, 108) * mm});
            skLineSegment(sketch, "E93", {"start": v(15, 108) * mm, "end": v(33, 90) * mm});
            skLineSegment(sketch, "E94", {"start": v(-80, 0) * mm, "end": v(80, 0) * mm, "construction": true});
            skLineSegment(sketch, "E95.MirrorCS", {"start": v(15, -120) * mm, "end": v(15, -108) * mm});
            skLineSegment(sketch, "E96.MirrorCS", {"start": v(15, -108) * mm, "end": v(33, -90) * mm});
            skArc(sketch, "E97.MirrorCS", {"start": v(-15, -120) * mm, "mid": v(0, -135) * mm, "end": v(15, -120) * mm});
            skLineSegment(sketch, "E98.MirrorCS", {"start": v(-15, -108) * mm, "end": v(-15, -120) * mm});
            skLineSegment(sketch, "E99.MirrorCS", {"start": v(-33, -90) * mm, "end": v(-15, -108) * mm});
            skCircle(sketch, "E100.MirrorC", {"center": v(0, -120) * mm, "radius": 6 * mm});
            skLineSegment(sketch, "E101.MirrorCS", {"start": v(0, -90) * mm, "end": v(0, -120) * mm, "construction": true});
            skSolve(sketch);
        }
        {
            var Q0;
            {var subQ1=sQuery(id+"F16.wireOp",EDGE,"E79.0.1");Q0=makeQuery(id+"F16.imprint","IMPRINT",FACE,{"disambiguationData":[TD([[makeQuery(id+"F16.imprint","IMPRINT",EDGE,{"derivedFrom":subQ1}),1.0]])]});}
            var Q1;
            Q1=makeQuery(id+"F16.imprint","IMPRINT",FACE,{"disambiguationData":[TD([[makeQuery(id+"F16.imprint","IMPRINT",EDGE,{"derivedFrom":sQuery(id+"F16.wireOp",EDGE,"E95.MirrorCS")}),1.0]])]});
            var Q2;
            Q2=makeQuery(id+"F16.imprint","IMPRINT",FACE,{"disambiguationData":[TD([[makeQuery(id+"F16.imprint","IMPRINT",EDGE,{"derivedFrom":sQuery(id+"F16.wireOp",EDGE,"E88")}),-1.0]])]});
            var Q3;
            Q3=makeQuery(id+"F2.opExtrude","CAP_FACE",FACE,{"disambiguationData":[OSD([sQuery(id+"F0.wireOp",EDGE,"E12"),sQuery(id+"F0.wireOp",EDGE,"E13"),sQuery(id+"F0.wireOp",EDGE,"E14"),sQuery(id+"F0.wireOp",EDGE,"E15"),sQuery(id+"F0.wireOp",EDGE,"E17.filletArc"),sQuery(id+"F0.wireOp",EDGE,"E18.filletArc"),sQuery(id+"F0.wireOp",EDGE,"E19.filletArc"),sQuery(id+"F0.wireOp",EDGE,"E20.filletArc"),sQuery(id+"F0.wireOp",EDGE,"E25.0"),sQuery(id+"F0.wireOp",EDGE,"E25.1"),sQuery(id+"F0.wireOp",EDGE,"E25.2"),sQuery(id+"F0.wireOp",EDGE,"E25.3"),sQuery(id+"F0.wireOp",EDGE,"E25.4"),sQuery(id+"F0.wireOp",EDGE,"E25.5"),sQuery(id+"F0.wireOp",EDGE,"E25.6"),sQuery(id+"F0.wireOp",EDGE,"E25.7")])],"isStart":false});
            extrude(context, id + "F17", {"entities" : qUnion([Q0, Q1, Q2]), "endBound" : BoundingType.UP_TO_SURFACE, "endBoundEntityFace" : qUnion([Q3]), "depth" : 25 * mm});
        }
    });
